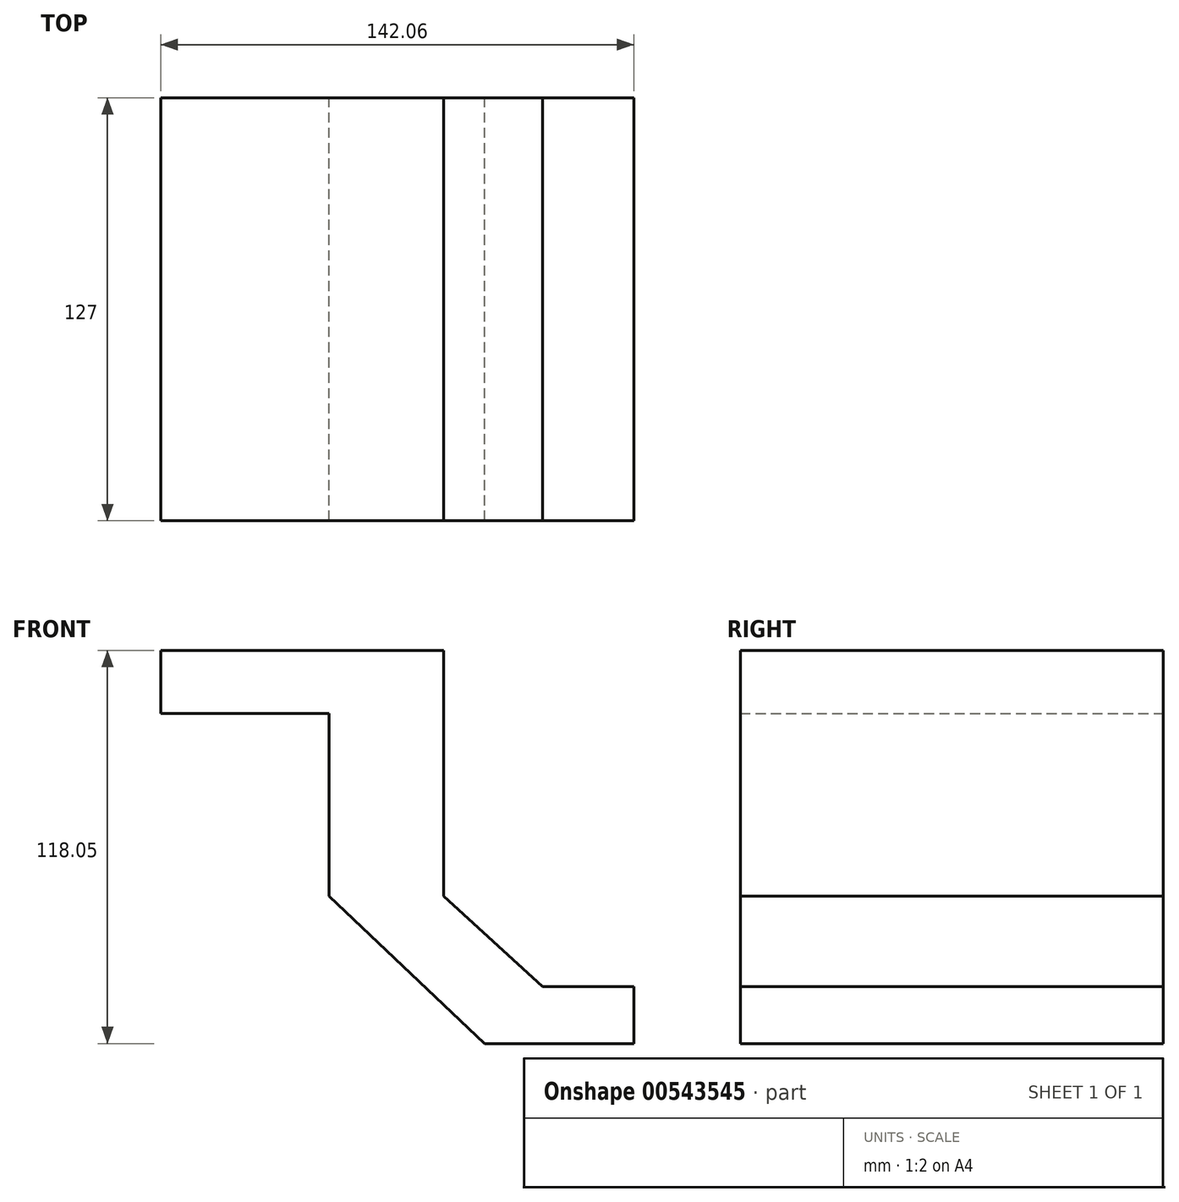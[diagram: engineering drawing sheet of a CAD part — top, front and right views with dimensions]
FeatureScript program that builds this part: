
annotation { "Feature Type Name" : "Feature", "Feature Type Description" : "" }
export const myFeature = defineFeature(function(context is Context, id is Id, definition is map)
    precondition{}
    {
        {
            var Q0;
            Q0=qCreatedBy(makeId("Front.planeOp"),FACE);
            var sketch = newSketch(context, id + "F0", { "sketchPlane" : qUnion([Q0])});
            skLineSegment(sketch, "E0", {"start": v(-142.06, 101) * mm, "end": v(-57.17, 101) * mm});
            skLineSegment(sketch, "E1", {"start": v(-57.17, 101) * mm, "end": v(-57.17, 27.27) * mm});
            skLineSegment(sketch, "E2", {"start": v(-57.17, 27.27) * mm, "end": v(-27.42, 0) * mm});
            skLineSegment(sketch, "E3", {"start": v(-27.42, 0) * mm, "end": v(0, 0) * mm});
            skLineSegment(sketch, "E4", {"start": v(0, 0) * mm, "end": v(0, -17.04) * mm});
            skLineSegment(sketch, "E5", {"start": v(0, -17.04) * mm, "end": v(-44.77, -17.04) * mm});
            skLineSegment(sketch, "E6", {"start": v(-44.77, -17.04) * mm, "end": v(-91.56, 27.27) * mm});
            skLineSegment(sketch, "E7", {"start": v(-91.56, 27.27) * mm, "end": v(-91.56, 82.1) * mm});
            skLineSegment(sketch, "E8", {"start": v(-91.56, 82.1) * mm, "end": v(-142.06, 82.1) * mm});
            skLineSegment(sketch, "E9", {"start": v(-142.06, 82.1) * mm, "end": v(-142.06, 101) * mm});
            skSolve(sketch);
        }
        {
            var Q0;
            Q0=makeQuery(id+"F0.imprint","IMPRINT",FACE,{"disambiguationData":[TD([[makeQuery(id+"F0.imprint","IMPRINT",EDGE,{"derivedFrom":sQuery(id+"F0.wireOp",EDGE,"E0")}),-1.0]])]});
            extrude(context, id + "F1", {"entities" : qUnion([Q0]), "depth" : 127 * mm, "offsetDistance" : 25.4 * mm});
        }
    });
